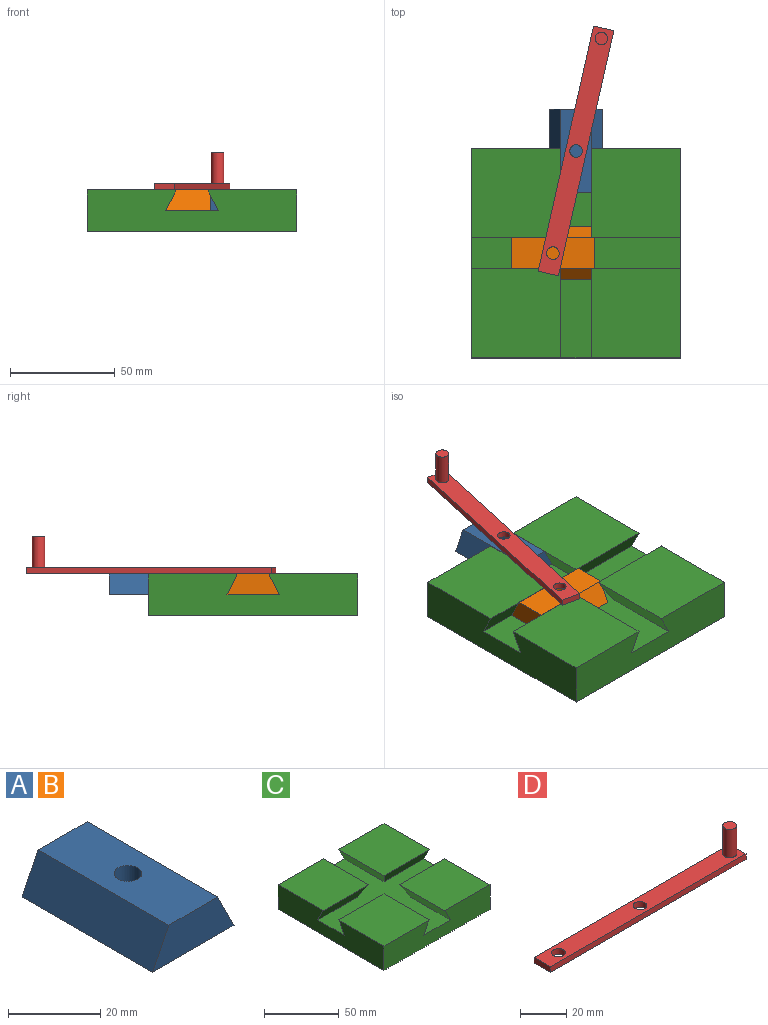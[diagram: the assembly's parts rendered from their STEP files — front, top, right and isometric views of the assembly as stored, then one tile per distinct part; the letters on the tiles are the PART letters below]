
ASSEMBLY  parts=4 mates=4
PART A: 8 faces, bbox 25x40x10 mm
  f0: plane 40x10mm, normal (-0.89,0,0.45), area 447.2mm2, adj f1,f3,f4,f5
  f1: plane 40x25mm, normal (0,0,-1), area 1000mm2, adj f0,f2,f4,f5
  f2: plane 40x10mm, normal (0.89,0,0.45), area 447.2mm2, adj f1,f3,f4,f5
  f3: plane 40x15mm, normal (0,0,1), area 571.7mm2, adj f0,f2,f4,f5,f6
  f4: plane 25x10mm, normal (0,-1,0), area 200mm2, adj f0,f1,f2,f3
  f5: plane 25x10mm, normal (0,1,0), area 200mm2, adj f0,f1,f2,f3
  f6: cylinder r=3mm len=6mm, axis (0,0,1), area 94.2mm2, adj f3,f7
  f7: plane 6x6mm, normal (0,0,1), area 28.3mm2, adj f6
PART B: same geometry as A
PART C: 18 faces, bbox 100x100x20 mm
  f0: plane 42.5x42.5mm, normal (0,0,1), area 1806.3mm2, adj f2,f7,f13,f15
  f1: plane 42.5x42.5mm, normal (0,0,1), area 1806.3mm2, adj f7,f8,f11,f17
  f2: plane 100x20mm, normal (1,0,0), area 1800mm2, adj f0,f5,f6,f7,f9,f12,f14,f15
  f3: plane 42.5x10mm, normal (0.89,0,-0.45), area 447.2mm2, adj f6,f10,f12,f16
  f4: plane 42.5x10mm, normal (-0.89,0,-0.45), area 447.2mm2, adj f5,f6,f12,f14
  f5: plane 42.5x42.5mm, normal (0,0,1), area 1806.3mm2, adj f2,f4,f6,f14
  f6: plane 100x20mm, normal (0,-1,0), area 1800mm2, adj f2,f3,f4,f5,f8,f9,f10,f12
  f7: plane 100x20mm, normal (0,1,0), area 1800mm2, adj f0,f1,f2,f8,f9,f11,f12,f13
  f8: plane 100x20mm, normal (-1,0,0), area 1800mm2, adj f1,f6,f7,f9,f10,f12,f16,f17
  f9: plane 100x100mm, normal (0,0,-1), area 10000mm2, adj f2,f6,f7,f8
  f10: plane 42.5x42.5mm, normal (0,0,1), area 1806.3mm2, adj f3,f6,f8,f16
  f11: plane 42.5x10mm, normal (0.89,0,-0.45), area 447.2mm2, adj f1,f7,f12,f17
  f12: plane 100x100mm, normal (0,0,1), area 4375mm2, adj f2,f3,f4,f6,f7,f8,f11,f13
  f13: plane 42.5x10mm, normal (-0.89,0,-0.45), area 447.2mm2, adj f0,f7,f12,f15
  f14: plane 42.5x10mm, normal (0,0.89,-0.45), area 447.2mm2, adj f2,f4,f5,f12
  f15: plane 42.5x10mm, normal (0,-0.89,-0.45), area 447.2mm2, adj f0,f2,f12,f13
  f16: plane 42.5x10mm, normal (0,0.89,-0.45), area 447.2mm2, adj f3,f8,f10,f12
  f17: plane 42.5x10mm, normal (0,-0.89,-0.45), area 447.2mm2, adj f1,f8,f11,f12
PART D: 10 faces, bbox 120x10x18 mm
  f0: plane 120x10mm, normal (0,0,-1), area 1143.5mm2, adj f1,f3,f4,f5,f6,f7
  f1: plane 120x3mm, normal (0,1,0), area 360mm2, adj f0,f2,f4,f5
  f2: plane 120x10mm, normal (0,0,1), area 1115.2mm2, adj f1,f3,f4,f5,f6,f7,f8
  f3: plane 120x3mm, normal (0,-1,0), area 360mm2, adj f0,f2,f4,f5
  f4: plane 10x3mm, normal (1,0,0), area 30mm2, adj f0,f1,f2,f3
  f5: plane 10x3mm, normal (-1,0,0), area 30mm2, adj f0,f1,f2,f3
  f6: cylinder r=3mm len=6mm, axis (0,0,1), area 56.5mm2, adj f0,f2
  f7: cylinder r=3mm len=6mm, axis (0,0,1), area 56.5mm2, adj f0,f2
  f8: cylinder r=3mm len=15mm, axis (0,0,-1), area 282.7mm2, adj f2,f9
  f9: plane 6x6mm, normal (0,0,1), area 28.3mm2, adj f8
PLACE A t=(0,48.77,0)mm
PLACE B rot(axis=(0,0,-1),90deg) t=(-11.01,0,0)mm
PLACE C at identity fixed
PLACE D rot(axis=(0,0,1),77.3deg) t=(-13.21,-9.75,1.5)mm
MATE revolute B.f6 <-> D.f7  axis (0,0,1) through (-11.01,0,0)mm
MATE slider A.f4 <-> C.f6  axis (0,-1,0) through (12.5,28.77,-10)mm
MATE revolute A.f6 <-> D.f6  axis (0,0,1) through (0,48.77,0)mm
MATE slider B.f5 <-> C.f2  axis (1,0,0) through (8.99,-12.5,-10)mm
